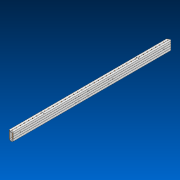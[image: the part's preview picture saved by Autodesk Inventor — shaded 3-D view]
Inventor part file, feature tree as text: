
AUTODESK INVENTOR PART (.ipt)
format: ipt  version: 2022.2 (Build 262287000, 287)  size: 717,824 bytes
history: native  units: in
note: dims shown in document units (in); Inventor stores cm internally (conversion verified against a paired STEP export)
features: other x51, reference x14, sketch x6, extrude x5, pattern_linear x1, hole x1
ambient origin geometry x8: Origin, YZ Plane, XZ Plane, XY Plane, X Axis, Y Axis, Z Axis, Center Point
bodies: Solid1 (feature_tree)
feature tree (78):
  extrude  "Extrusion1"  Depth=2.0in
  other  "Work Axis1"
  pattern_linear  "Rectangular Pattern1"  Count1=39  [1 undecoded]
  extrude  "Extrusion2"  Depth=1.0in
  extrude  "Extrusion3"  Depth=1.0in
  extrude  "Extrusion4"  Depth=1.0in
  hole  "Hole1"  [1 undecoded]
  extrude  "Extrusion5"  TaperAngle=0.0deg  [1 undecoded]
  sketch  "Sketch1"  dims[d0=1.0in d1=2.0in]
  other  "Work Axis2"
  other  "Work Axis3"
  other  "Work Axis4"
  other  "Work Axis5"
  other  "Work Axis6"
  other  "Work Axis7"
  other  "Work Axis8"
  other  "Work Axis9"
  other  "Work Axis10"
  other  "Work Axis60"
  other  "Work Axis61"
  other  "Work Axis62"
  other  "Work Axis63"
  other  "Work Axis64"
  other  "Work Axis65"
  other  "Work Axis66"
  other  "Work Axis67"
  other  "Work Axis68"
  other  "Work Axis69"
  other  "Work Axis70"
  other  "Work Axis71"
  other  "Work Axis72"
  other  "Work Axis73"
  other  "Work Axis74"
  other  "Work Axis75"
  other  "Work Axis76"
  other  "Work Axis77"
  other  "Work Axis78"
  other  "Work Axis79"
  other  "Work Axis80"
  other  "Work Axis81"
  other  "Work Axis82"
  other  "Work Axis83"
  other  "Work Axis84"
  other  "Work Axis85"
  other  "Work Axis86"
  other  "Work Axis87"
  other  "Work Axis88"
  sketch  "Sketch3"  dims[d2=20.0in]
  sketch  "Sketch4"  dims[d3=0.0in d4=15.3543in]
  reference  "Reference1"
  reference  "Reference2"
  reference  "Reference3"
  reference  "Reference4"
  reference  "Reference5"
  reference  "Reference6"
  reference  "Reference7"
  reference  "Reference8"
  sketch  "Sketch5"  dims[d6=1.0in d8=0.17in]
  reference  "Reference9"
  reference  "Reference10"
  reference  "Reference11"
  reference  "Reference12"
  sketch  "Sketch6"  dims[d9=0.0in d10=0.0in d11=1.0in]
  sketch  "Sketch7"  dims[d12=2.2325in d13=6.0in d14=0.0in d15=0.0in d16=0.0in d17=0.0in d18=1.0in d19=1.5in d20=0.17in d21=0.2362in d22=0.1575in d23=0.0787in d24=90.0deg d25=0.315in d26=0.8108in d27=0.0in d28=0.0in]
  reference  "Reference13"
  reference  "Reference14"
  other  "Cut-Extrude2"
  parser-record x2  (decoder bookkeeping rows leaked as tree rows — omitted from the tree; the rows remain in map.json)
  other  "Chassis.iam"
  other  "VersaFrame 45 Degree Gusset (217-3552):8"
  other  "VersaFrame 45 Degree Gusset (217-3552):3"
  other  "VersaFrame 135 Degree Gusset Modifed 2(217-3556):1"
  other  "VersaFrame 135 Degree Gusset Modifed 2(217-3556):3"
  other  "Robot.iam"
  other  "Tower:1"
  other  "1 x 1 x 0.040 x 26 Tower Stablizer Pre-Drilled VersaFrame Aluminum Tube Stock Cut (217-3426):3"
  other  "1 x 1 x 0.040 x 26 Tower Stablizer Pre-Drilled VersaFrame Aluminum Tube Stock Cut (217-3426):4"
note: 3 required parameter values undecoded (feature->parameter linkage not recoverable at this tier; creation-order binding heuristic only, values carry confidence <= 0.55)
note: 2 file-system paths scrubbed to <path> (originals preserved in map.json)
